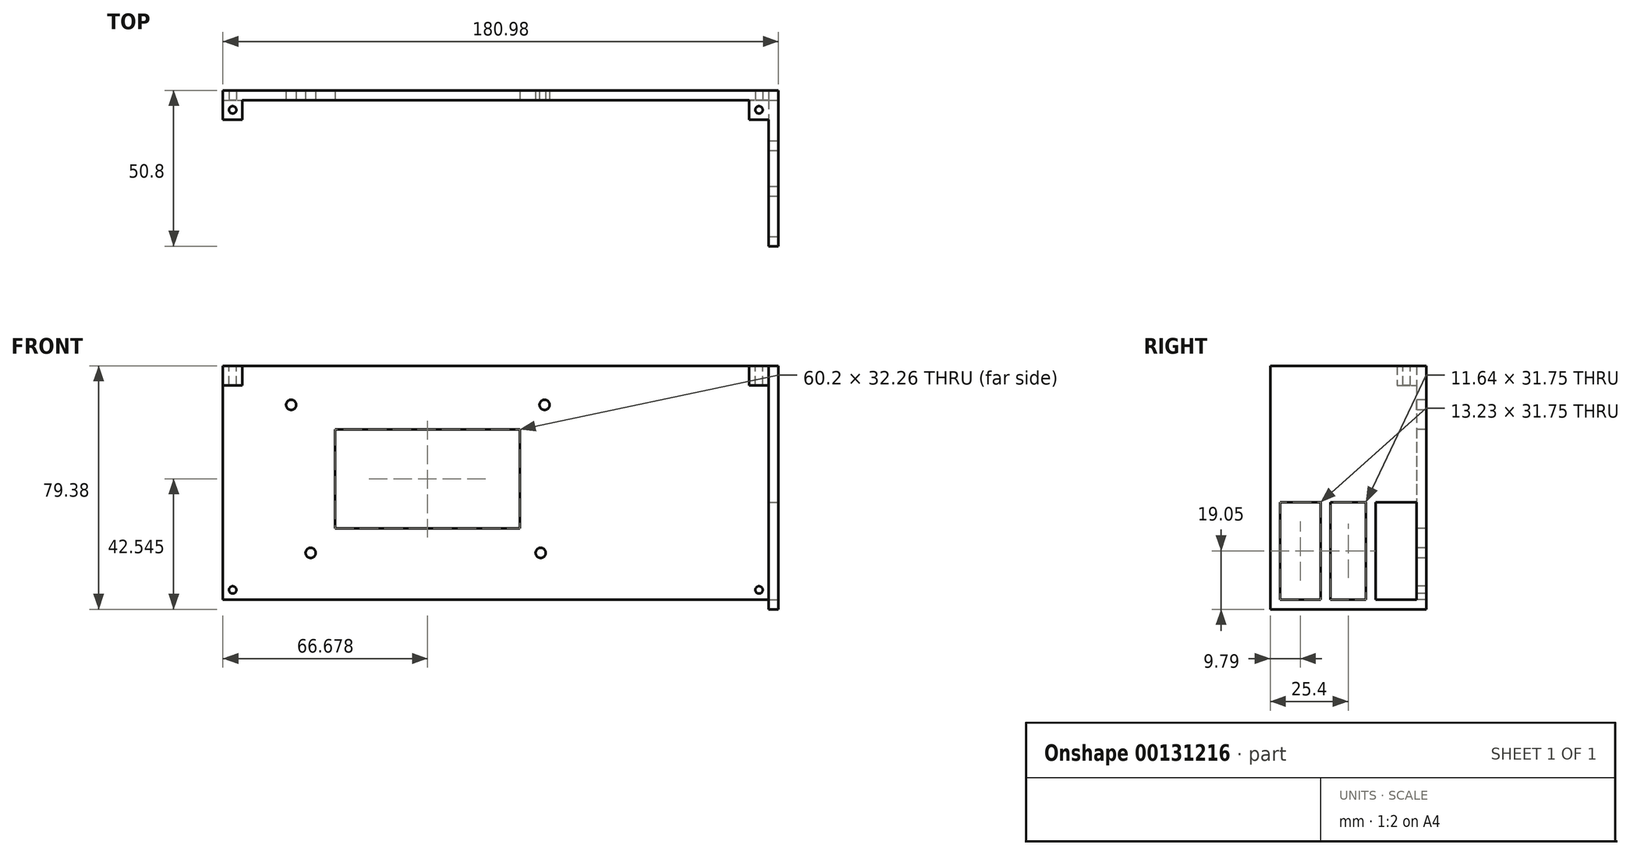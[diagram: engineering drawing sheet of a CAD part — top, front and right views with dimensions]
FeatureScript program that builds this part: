
annotation { "Feature Type Name" : "Feature", "Feature Type Description" : "" }
export const myFeature = defineFeature(function(context is Context, id is Id, definition is map)
    precondition{}
    {
        {
            var Q0;
            Q0=qCreatedBy(makeId("Top.planeOp"),FACE);
            var sketch = newSketch(context, id + "F0", { "sketchPlane" : qUnion([Q0])});
            skLineSegment(sketch, "E0.bottom", {"start": v(-95.97, 25.4) * mm, "end": v(88.18, 25.4) * mm});
            skLineSegment(sketch, "E0.top", {"start": v(-95.97, -25.4) * mm, "end": v(88.18, -25.4) * mm});
            skLineSegment(sketch, "E0.left", {"start": v(-95.97, 25.4) * mm, "end": v(-95.97, -25.4) * mm});
            skLineSegment(sketch, "E0.right", {"start": v(88.18, 25.4) * mm, "end": v(88.18, -25.4) * mm});
            skPoint(sketch, "E0.middle", {"position": v(-3.9, 0) * mm});
            skSolve(sketch);
        }
        {
            var Q0;
            Q0=makeQuery(id+"F0.imprint","IMPRINT",FACE,{"disambiguationData":[TD([[makeQuery(id+"F0.imprint","IMPRINT",EDGE,{"derivedFrom":sQuery(id+"F0.wireOp",EDGE,"E0.bottom")}),-1.0]])]});
            extrude(context, id + "F1", {"entities" : qUnion([Q0]), "depth" : 3.17 * mm});
        }
        {
            var Q0;
            Q0=makeQuery(id+"F1.opExtrude","CAP_FACE",FACE,{"disambiguationData":[OSD([sQuery(id+"F0.wireOp",EDGE,"E0.bottom"),sQuery(id+"F0.wireOp",EDGE,"E0.top"),sQuery(id+"F0.wireOp",EDGE,"E0.left"),sQuery(id+"F0.wireOp",EDGE,"E0.right")])],"isStart":false});
            var sketch = newSketch(context, id + "F2", { "sketchPlane" : qUnion([Q0])});
            skPoint(sketch, "E1", {"position": v(-78.9, 9.53) * mm});
            skPoint(sketch, "E2", {"position": v(71.1, 9.53) * mm});
            skPoint(sketch, "E3", {"position": v(71.1, -15.47) * mm});
            skPoint(sketch, "E4", {"position": v(-78.9, -15.47) * mm});
            skLineSegment(sketch, "E5", {"start": v(-78.9, 9.53) * mm, "end": v(-95.97, 9.53) * mm, "construction": true});
            skLineSegment(sketch, "E6", {"start": v(71.1, 9.53) * mm, "end": v(88.18, 9.53) * mm, "construction": true});
            skPoint(sketch, "E6.endSnap0", {"position": v(88.18, 0) * mm});
            skSolve(sketch);
        }
        {
            var Q0;
            Q0=sQuery(id+"F2.wireOp",VERTEX,"E1");
            var Q1;
            Q1=sQuery(id+"F2.wireOp",VERTEX,"E4");
            var Q2;
            Q2=sQuery(id+"F2.wireOp",VERTEX,"E3");
            var Q3;
            Q3=sQuery(id+"F2.wireOp",VERTEX,"E2");
            var Q4;
            Q4=makeQuery(id+"F1.opExtrude","SWEPT_BODY",BODY,{"disambiguationData":[OSD([sQuery(id+"F0.wireOp",EDGE,"E0.bottom"),sQuery(id+"F0.wireOp",EDGE,"E0.top"),sQuery(id+"F0.wireOp",EDGE,"E0.left"),sQuery(id+"F0.wireOp",EDGE,"E0.right")])]});
            hole(context, id + "F3", {"style" : HoleStyle.SIMPLE, "endStyle" : HoleEndStyle.THROUGH, "standardTappedOrClearance" : lookupTablePath({ "standard" : "ISO", "engagement" : "75%", "pitch" : "0.75 mm", "size" : "M4", "type" : "Tapped" }), "standardBlindInLast" : lookupTablePath({ "standard" : "ISO", "engagement" : "75%", "pitch" : "0.75 mm", "size" : "M4", "type" : "Tapped" }), "holeDiameter" : 3.2 * mm, "locations" : qUnion([Q0, Q1, Q2, Q3]), "scope" : qUnion([Q4]), "isTappedThrough" : true, "showTappedDepth" : true});
        }
        {
            var Q0;
            Q0=makeQuery(id+"F1.opExtrude","CAP_FACE",FACE,{"disambiguationData":[OSD([sQuery(id+"F0.wireOp",EDGE,"E0.bottom"),sQuery(id+"F0.wireOp",EDGE,"E0.top"),sQuery(id+"F0.wireOp",EDGE,"E0.left"),sQuery(id+"F0.wireOp",EDGE,"E0.right")])],"isStart":false});
            var sketch = newSketch(context, id + "F4", { "sketchPlane" : qUnion([Q0])});
            skLineSegment(sketch, "E7.bottom", {"start": v(-95.97, 25.4) * mm, "end": v(88.18, 25.4) * mm});
            skLineSegment(sketch, "E7.top", {"start": v(-95.97, 22.23) * mm, "end": v(88.18, 22.23) * mm});
            skLineSegment(sketch, "E7.left", {"start": v(-95.97, 25.4) * mm, "end": v(-95.97, 22.23) * mm});
            skLineSegment(sketch, "E7.right", {"start": v(88.18, 25.4) * mm, "end": v(88.18, 22.23) * mm});
            skSolve(sketch);
        }
        {
            var Q0;
            Q0=makeQuery(id+"F4.imprint","IMPRINT",FACE,{"disambiguationData":[TD([[makeQuery(id+"F4.imprint","IMPRINT",EDGE,{"derivedFrom":sQuery(id+"F4.wireOp",EDGE,"E7.bottom")}),-1.0]])]});
            extrude(context, id + "F5", {"entities" : qUnion([Q0]), "operationType" : NewBodyOperationType.ADD, "depth" : 76.2 * mm});
        }
        {
            var Q0;
            Q0=makeQuery(id+"F5.opExtrude","SWEPT_FACE",FACE,{"disambiguationData":[OSD([sQuery(id+"F4.wireOp",EDGE,"E7.top")])]});
            var sketch = newSketch(context, id + "F6", { "sketchPlane" : qUnion([Q0])});
            skPoint(sketch, "E8", {"position": v(-70.57, 66.67) * mm});
            skPoint(sketch, "E9", {"position": v(11.98, 66.67) * mm});
            skPoint(sketch, "E10", {"position": v(-64.22, 18.41) * mm});
            skPoint(sketch, "E11", {"position": v(10.7, 18.42) * mm});
            skSolve(sketch);
        }
        {
            var Q0;
            Q0=sQuery(id+"F6.wireOp",VERTEX,"E8");
            var Q1;
            Q1=sQuery(id+"F6.wireOp",VERTEX,"E9");
            var Q2;
            Q2=sQuery(id+"F6.wireOp",VERTEX,"E11");
            var Q3;
            Q3=sQuery(id+"F6.wireOp",VERTEX,"E10");
            var Q4;
            Q4=makeQuery(id+"F1.opExtrude","SWEPT_BODY",BODY,{"disambiguationData":[OSD([sQuery(id+"F0.wireOp",EDGE,"E0.bottom"),sQuery(id+"F0.wireOp",EDGE,"E0.top"),sQuery(id+"F0.wireOp",EDGE,"E0.left"),sQuery(id+"F0.wireOp",EDGE,"E0.right")])]});
            hole(context, id + "F7", {"style" : HoleStyle.SIMPLE, "endStyle" : HoleEndStyle.THROUGH, "standardTappedOrClearance" : lookupTablePath({ "standard" : "ISO", "fit" : "Normal", "size" : "M3", "type" : "Clearance" }), "standardBlindInLast" : lookupTablePath({ "fit" : "Standard", "standard" : "ISO", "size" : "M3", "type" : "Clearance" }), "holeDiameter" : 3.3 * mm, "locations" : qUnion([Q0, Q1, Q2, Q3]), "scope" : qUnion([Q4]), "isTappedThrough" : true});
        }
        {
            var Q0;
            Q0=makeQuery(id+"F1.opExtrude","CAP_FACE",FACE,{"disambiguationData":[OSD([sQuery(id+"F0.wireOp",EDGE,"E0.bottom"),sQuery(id+"F0.wireOp",EDGE,"E0.top"),sQuery(id+"F0.wireOp",EDGE,"E0.left"),sQuery(id+"F0.wireOp",EDGE,"E0.right")])],"isStart":false});
            var sketch = newSketch(context, id + "F8", { "sketchPlane" : qUnion([Q0])});
            skLineSegment(sketch, "E12.bottom", {"start": v(-95.97, 22.23) * mm, "end": v(-92.8, 22.23) * mm});
            skLineSegment(sketch, "E12.top", {"start": v(-95.97, -25.4) * mm, "end": v(-92.8, -25.4) * mm});
            skLineSegment(sketch, "E12.left", {"start": v(-95.97, 22.23) * mm, "end": v(-95.97, -25.4) * mm});
            skLineSegment(sketch, "E12.right", {"start": v(-92.8, 22.23) * mm, "end": v(-92.8, -25.4) * mm});
            skSolve(sketch);
        }
        {
            var Q0;
            Q0=makeQuery(id+"F8.imprint","IMPRINT",FACE,{"disambiguationData":[TD([[makeQuery(id+"F8.imprint","IMPRINT",EDGE,{"derivedFrom":sQuery(id+"F8.wireOp",EDGE,"E12.bottom")}),-1.0]])]});
            extrude(context, id + "F9", {"entities" : qUnion([Q0]), "operationType" : NewBodyOperationType.ADD, "depth" : 76.2 * mm});
        }
        {
            var Q0;
            Q0=makeQuery(id+"F9.boolean.opBoolean","MERGE",FACE,{"derivedFrom":[makeQuery(id+"F5.boolean.opBoolean","MERGE",FACE,{"derivedFrom":[makeQuery(id+"F1.opExtrude","SWEPT_FACE",FACE,{"disambiguationData":[OSD([sQuery(id+"F0.wireOp",EDGE,"E0.left")])]}),makeQuery(id+"F5.opExtrude","SWEPT_FACE",FACE,{"disambiguationData":[OSD([sQuery(id+"F4.wireOp",EDGE,"E7.left")])]})]}),makeQuery(id+"F9.opExtrude","SWEPT_FACE",FACE,{"disambiguationData":[OSD([sQuery(id+"F8.wireOp",EDGE,"E12.left")])]})]});
            var sketch = newSketch(context, id + "F10", { "sketchPlane" : qUnion([Q0])});
            skLineSegment(sketch, "E13.bottom", {"start": v(3.18, 76.2) * mm, "end": v(22.23, 76.2) * mm});
            skLineSegment(sketch, "E13.top", {"start": v(3.18, 3.18) * mm, "end": v(22.23, 3.18) * mm});
            skLineSegment(sketch, "E13.left", {"start": v(3.18, 76.2) * mm, "end": v(3.18, 3.17) * mm});
            skLineSegment(sketch, "E13.right", {"start": v(22.23, 76.2) * mm, "end": v(22.23, 3.17) * mm});
            skLineSegment(sketch, "E14", {"start": v(3.18, 39.69) * mm, "end": v(22.23, 39.69) * mm});
            skLineSegment(sketch, "E15", {"start": v(3.18, 41.27) * mm, "end": v(22.23, 41.27) * mm});
            skLineSegment(sketch, "E16", {"start": v(3.18, 38.1) * mm, "end": v(22.23, 38.1) * mm});
            skSolve(sketch);
        }
        {
            var Q0;
            {var subQ0=sQuery(id+"F10.wireOp",EDGE,"E13.bottom");Q0=makeQuery(id+"F10.imprint","IMPRINT",FACE,{"disambiguationData":[TD([[makeQuery(id+"F10.imprint","IMPRINT",EDGE,{"derivedFrom":subQ0}),-1.0]])]});}
            var Q1;
            {var subQ0=sQuery(id+"F10.wireOp",EDGE,"E13.top");Q1=makeQuery(id+"F10.imprint","IMPRINT",FACE,{"disambiguationData":[TD([[makeQuery(id+"F10.imprint","IMPRINT",EDGE,{"derivedFrom":subQ0}),1.0]])]});}
            extrude(context, id + "F11", {"entities" : qUnion([Q0, Q1]), "operationType" : NewBodyOperationType.REMOVE, "endBound" : BoundingType.UP_TO_NEXT, "oppositeDirection" : true, "depth" : 25.4 * mm});
        }
        {
            var Q0;
            Q0=makeQuery(id+"F11.boolean.opBoolean","MERGE",FACE,{"derivedFrom":[makeQuery(id+"F1.opExtrude","CAP_FACE",FACE,{"disambiguationData":[OSD([sQuery(id+"F0.wireOp",EDGE,"E0.bottom"),sQuery(id+"F0.wireOp",EDGE,"E0.top"),sQuery(id+"F0.wireOp",EDGE,"E0.left"),sQuery(id+"F0.wireOp",EDGE,"E0.right")])],"isStart":false}),makeQuery(id+"F11.opExtrude","SWEPT_FACE",FACE,{"disambiguationData":[OSD([sQuery(id+"F10.wireOp",EDGE,"E13.top")])]})]});
            var sketch = newSketch(context, id + "F12", { "sketchPlane" : qUnion([Q0])});
            skLineSegment(sketch, "E17.bottom", {"start": v(88.18, 22.23) * mm, "end": v(85, 22.23) * mm});
            skLineSegment(sketch, "E17.top", {"start": v(88.18, -25.4) * mm, "end": v(85, -25.4) * mm});
            skLineSegment(sketch, "E17.left", {"start": v(88.18, 22.23) * mm, "end": v(88.18, -25.4) * mm});
            skLineSegment(sketch, "E17.right", {"start": v(85, 22.23) * mm, "end": v(85, -25.4) * mm});
            skSolve(sketch);
        }
        {
            var Q0;
            Q0=makeQuery(id+"F12.imprint","IMPRINT",FACE,{"disambiguationData":[TD([[makeQuery(id+"F12.imprint","IMPRINT",EDGE,{"derivedFrom":sQuery(id+"F12.wireOp",EDGE,"E17.bottom")}),-1.0]])]});
            extrude(context, id + "F13", {"entities" : qUnion([Q0]), "operationType" : NewBodyOperationType.ADD, "depth" : 76.2 * mm});
        }
        {
            var Q0;
            Q0=makeQuery(id+"F13.boolean.opBoolean","MERGE",FACE,{"derivedFrom":[makeQuery(id+"F5.boolean.opBoolean","MERGE",FACE,{"derivedFrom":[makeQuery(id+"F1.opExtrude","SWEPT_FACE",FACE,{"disambiguationData":[OSD([sQuery(id+"F0.wireOp",EDGE,"E0.right")])]}),makeQuery(id+"F5.opExtrude","SWEPT_FACE",FACE,{"disambiguationData":[OSD([sQuery(id+"F4.wireOp",EDGE,"E7.right")])]})]}),makeQuery(id+"F13.opExtrude","SWEPT_FACE",FACE,{"disambiguationData":[OSD([sQuery(id+"F12.wireOp",EDGE,"E17.left")])]})]});
            var sketch = newSketch(context, id + "F14", { "sketchPlane" : qUnion([Q0])});
            skLineSegment(sketch, "E18.bottom", {"start": v(-22.22, 3.17) * mm, "end": v(22.23, 3.18) * mm});
            skLineSegment(sketch, "E18.top", {"start": v(-22.22, 34.92) * mm, "end": v(22.23, 34.93) * mm});
            skLineSegment(sketch, "E18.left", {"start": v(-22.22, 3.17) * mm, "end": v(-22.22, 34.92) * mm});
            skLineSegment(sketch, "E18.right", {"start": v(22.23, 3.17) * mm, "end": v(22.23, 34.92) * mm});
            skLineSegment(sketch, "E19", {"start": v(-7.4, 34.92) * mm, "end": v(-7.4, 3.18) * mm, "construction": true});
            skLineSegment(sketch, "E20", {"start": v(7.4, 34.92) * mm, "end": v(7.4, 3.18) * mm, "construction": true});
            skLineSegment(sketch, "E21", {"start": v(-22.22, 19.05) * mm, "end": v(-7.4, 19.05) * mm, "construction": true});
            skLineSegment(sketch, "E22", {"start": v(-7.4, 19.05) * mm, "end": v(7.4, 19.05) * mm, "construction": true});
            skLineSegment(sketch, "E23", {"start": v(7.4, 19.05) * mm, "end": v(22.23, 19.05) * mm, "construction": true});
            skLineSegment(sketch, "E24.bottom", {"start": v(-9, 34.92) * mm, "end": v(-5.82, 34.92) * mm});
            skLineSegment(sketch, "E24.top", {"start": v(-9, 3.17) * mm, "end": v(-5.82, 3.17) * mm});
            skLineSegment(sketch, "E24.left", {"start": v(-9, 34.92) * mm, "end": v(-9, 3.17) * mm});
            skLineSegment(sketch, "E24.right", {"start": v(-5.82, 34.92) * mm, "end": v(-5.82, 3.17) * mm});
            skPoint(sketch, "E24.middle", {"position": v(-7.4, 19.05) * mm});
            skLineSegment(sketch, "E25.bottom", {"start": v(5.82, 34.92) * mm, "end": v(9, 34.92) * mm});
            skLineSegment(sketch, "E25.top", {"start": v(5.82, 3.17) * mm, "end": v(9, 3.17) * mm});
            skLineSegment(sketch, "E25.left", {"start": v(5.82, 34.92) * mm, "end": v(5.82, 3.17) * mm});
            skLineSegment(sketch, "E25.right", {"start": v(9, 34.92) * mm, "end": v(9, 3.17) * mm});
            skPoint(sketch, "E25.middle", {"position": v(7.4, 19.05) * mm});
            skSolve(sketch);
        }
        {
            var Q0;
            {var subQ0=sQuery(id+"F14.wireOp",EDGE,"E18.left");Q0=makeQuery(id+"F14.imprint","IMPRINT",FACE,{"disambiguationData":[TD([[makeQuery(id+"F14.imprint","IMPRINT",EDGE,{"derivedFrom":subQ0}),-1.0]])]});}
            var Q1;
            {var subQ0=sQuery(id+"F14.wireOp",EDGE,"E24.right");Q1=makeQuery(id+"F14.imprint","IMPRINT",FACE,{"disambiguationData":[TD([[makeQuery(id+"F14.imprint","IMPRINT",EDGE,{"derivedFrom":subQ0}),1.0]])]});}
            var Q2;
            {var subQ0=sQuery(id+"F14.wireOp",EDGE,"E18.right");Q2=makeQuery(id+"F14.imprint","IMPRINT",FACE,{"disambiguationData":[TD([[makeQuery(id+"F14.imprint","IMPRINT",EDGE,{"derivedFrom":subQ0}),1.0]])]});}
            extrude(context, id + "F15", {"entities" : qUnion([Q0, Q1, Q2]), "operationType" : NewBodyOperationType.REMOVE, "endBound" : BoundingType.UP_TO_NEXT, "oppositeDirection" : true, "depth" : 25.4 * mm});
        }
        {
            var Q0;
            Q0=makeQuery(id+"F15.boolean.opBoolean","MERGE",FACE,{"derivedFrom":[makeQuery(id+"F5.opExtrude","SWEPT_FACE",FACE,{"disambiguationData":[OSD([sQuery(id+"F4.wireOp",EDGE,"E7.top")])]}),makeQuery(id+"F15.opExtrude","SWEPT_FACE",FACE,{"disambiguationData":[OSD([sQuery(id+"F14.wireOp",EDGE,"E18.right")])]})]});
            var sketch = newSketch(context, id + "F16", { "sketchPlane" : qUnion([Q0])});
            skLineSegment(sketch, "E26.bottom", {"start": v(-92.8, 79.38) * mm, "end": v(-86.45, 79.38) * mm});
            skLineSegment(sketch, "E26.top", {"start": v(-92.8, 73.03) * mm, "end": v(-86.45, 73.03) * mm});
            skLineSegment(sketch, "E26.left", {"start": v(-92.8, 79.38) * mm, "end": v(-92.8, 73.03) * mm});
            skLineSegment(sketch, "E26.right", {"start": v(-86.45, 79.38) * mm, "end": v(-86.45, 73.03) * mm});
            skLineSegment(sketch, "E27.bottom", {"start": v(85, 79.38) * mm, "end": v(78.65, 79.38) * mm});
            skLineSegment(sketch, "E27.top", {"start": v(85, 73.03) * mm, "end": v(78.65, 73.03) * mm});
            skLineSegment(sketch, "E27.left", {"start": v(85, 79.38) * mm, "end": v(85, 73.03) * mm});
            skLineSegment(sketch, "E27.right", {"start": v(78.65, 79.38) * mm, "end": v(78.65, 73.03) * mm});
            skSolve(sketch);
        }
        {
            var Q0;
            Q0=makeQuery(id+"F16.imprint","IMPRINT",FACE,{"disambiguationData":[TD([[makeQuery(id+"F16.imprint","IMPRINT",EDGE,{"derivedFrom":sQuery(id+"F16.wireOp",EDGE,"E26.bottom")}),-1.0]])]});
            var Q1;
            Q1=makeQuery(id+"F16.imprint","IMPRINT",FACE,{"disambiguationData":[TD([[makeQuery(id+"F16.imprint","IMPRINT",EDGE,{"derivedFrom":sQuery(id+"F16.wireOp",EDGE,"E26.bottom")}),-1.0]])]});
            var Q2;
            Q2=makeQuery(id+"F16.imprint","IMPRINT",FACE,{"disambiguationData":[TD([[makeQuery(id+"F16.imprint","IMPRINT",EDGE,{"derivedFrom":sQuery(id+"F16.wireOp",EDGE,"E27.bottom")}),-1.0]])]});
            extrude(context, id + "F17", {"entities" : qUnion([Q0, Q1, Q2]), "operationType" : NewBodyOperationType.ADD, "depth" : 6.35 * mm});
        }
        {
            var Q0;
            Q0=makeQuery(id+"F17.boolean.opBoolean","MERGE",FACE,{"derivedFrom":[makeQuery(id+"F13.boolean.opBoolean","MERGE",FACE,{"derivedFrom":[makeQuery(id+"F9.boolean.opBoolean","MERGE",FACE,{"derivedFrom":[makeQuery(id+"F5.opExtrude","CAP_FACE",FACE,{"disambiguationData":[OSD([sQuery(id+"F4.wireOp",EDGE,"E7.bottom"),sQuery(id+"F4.wireOp",EDGE,"E7.top"),sQuery(id+"F4.wireOp",EDGE,"E7.left"),sQuery(id+"F4.wireOp",EDGE,"E7.right")])],"isStart":false}),makeQuery(id+"F9.opExtrude","CAP_FACE",FACE,{"disambiguationData":[OSD([sQuery(id+"F8.wireOp",EDGE,"E12.bottom"),sQuery(id+"F8.wireOp",EDGE,"E12.top"),sQuery(id+"F8.wireOp",EDGE,"E12.left"),sQuery(id+"F8.wireOp",EDGE,"E12.right")])],"isStart":false})]}),makeQuery(id+"F13.opExtrude","CAP_FACE",FACE,{"disambiguationData":[OSD([sQuery(id+"F12.wireOp",EDGE,"E17.bottom"),sQuery(id+"F12.wireOp",EDGE,"E17.top"),sQuery(id+"F12.wireOp",EDGE,"E17.left"),sQuery(id+"F12.wireOp",EDGE,"E17.right")])],"isStart":false})]}),makeQuery(id+"F17.opExtrude","SWEPT_FACE",FACE,{"disambiguationData":[OSD([sQuery(id+"F16.wireOp",EDGE,"E26.bottom")])]}),makeQuery(id+"F17.opExtrude","SWEPT_FACE",FACE,{"disambiguationData":[OSD([sQuery(id+"F16.wireOp",EDGE,"E27.bottom")])]})]});
            var sketch = newSketch(context, id + "F18", { "sketchPlane" : qUnion([Q0])});
            skPoint(sketch, "E28", {"position": v(-89.62, 19.05) * mm});
            skPoint(sketch, "E29", {"position": v(81.83, 19.05) * mm});
            skSolve(sketch);
        }
        {
            var Q0;
            Q0=sQuery(id+"F18.wireOp",VERTEX,"E28");
            var Q1;
            Q1=sQuery(id+"F18.wireOp",VERTEX,"E29");
            var Q2;
            Q2=makeQuery(id+"F1.opExtrude","SWEPT_BODY",BODY,{"disambiguationData":[OSD([sQuery(id+"F0.wireOp",EDGE,"E0.bottom"),sQuery(id+"F0.wireOp",EDGE,"E0.top"),sQuery(id+"F0.wireOp",EDGE,"E0.left"),sQuery(id+"F0.wireOp",EDGE,"E0.right")])]});
            hole(context, id + "F19", {"style" : HoleStyle.SIMPLE, "endStyle" : HoleEndStyle.BLIND, "standardTappedOrClearance" : lookupTablePath({ "standard" : "ISO", "engagement" : "75%", "pitch" : "0.6 mm", "size" : "M3", "type" : "Tapped" }), "standardBlindInLast" : lookupTablePath({ "standard" : "ISO", "engagement" : "75%", "pitch" : "0.6 mm", "size" : "M3", "type" : "Tapped" }), "holeDiameter" : 2.4 * mm, "holeDepth" : 12.7 * mm, "locations" : qUnion([Q0, Q1]), "scope" : qUnion([Q2])});
        }
        {
            var Q0;
            {var subQ0=sQuery(id+"F14.wireOp",EDGE,"E18.bottom");var subQ2=sQuery(id+"F14.wireOp",EDGE,"E24.top");Q0=makeQuery(id+"F15.boolean.opBoolean","MERGE",FACE,{"derivedFrom":[makeQuery(id+"F11.boolean.opBoolean","MERGE",FACE,{"derivedFrom":[makeQuery(id+"F1.opExtrude","CAP_FACE",FACE,{"disambiguationData":[OSD([sQuery(id+"F0.wireOp",EDGE,"E0.bottom"),sQuery(id+"F0.wireOp",EDGE,"E0.top"),sQuery(id+"F0.wireOp",EDGE,"E0.left"),sQuery(id+"F0.wireOp",EDGE,"E0.right")])],"isStart":false}),makeQuery(id+"F11.opExtrude","SWEPT_FACE",FACE,{"disambiguationData":[OSD([sQuery(id+"F10.wireOp",EDGE,"E13.top")])]})]}),makeQuery(id+"F15.opExtrude","SWEPT_FACE",FACE,{"disambiguationData":[OSD([subQ0]),TDD([makeQuery(id+"F14.imprint","IMPRINT",EDGE,{"disambiguationData":[TD([[makeQuery(id+"F14.imprint","INTERSECT",VERTEX,{"derivedFrom":[subQ0,sQuery(id+"F14.wireOp",EDGE,"E18.left")]}),-1.0]])],"derivedFrom":subQ0})])]}),makeQuery(id+"F15.opExtrude","SWEPT_FACE",FACE,{"disambiguationData":[OSD([subQ0]),TDD([makeQuery(id+"F14.imprint","IMPRINT",EDGE,{"disambiguationData":[TD([[makeQuery(id+"F14.imprint","INTERSECT",VERTEX,{"derivedFrom":[subQ0,subQ2,sQuery(id+"F14.wireOp",EDGE,"E24.right")]}),-1.0]])],"derivedFrom":subQ0})])]}),makeQuery(id+"F15.opExtrude","SWEPT_FACE",FACE,{"disambiguationData":[OSD([subQ0]),TDD([makeQuery(id+"F14.imprint","IMPRINT",EDGE,{"disambiguationData":[TD([[makeQuery(id+"F14.imprint","INTERSECT",VERTEX,{"derivedFrom":[subQ0,sQuery(id+"F14.wireOp",EDGE,"E18.right")]}),1.0]])],"derivedFrom":subQ0})])]})]});}
            var sketch = newSketch(context, id + "F20", { "sketchPlane" : qUnion([Q0])});
            skLineSegment(sketch, "E30.bottom", {"start": v(-64.6, -19.05) * mm, "end": v(56.8, -19.05) * mm});
            skLineSegment(sketch, "E30.top", {"start": v(-64.6, 15.88) * mm, "end": v(56.8, 15.88) * mm});
            skLineSegment(sketch, "E30.left", {"start": v(-64.6, -19.05) * mm, "end": v(-64.6, 15.88) * mm});
            skLineSegment(sketch, "E30.right", {"start": v(56.8, -19.05) * mm, "end": v(56.8, 15.88) * mm});
            skSolve(sketch);
        }
        {
            var Q0;
            Q0=makeQuery(id+"F20.imprint","IMPRINT",FACE,{"disambiguationData":[TD([[makeQuery(id+"F20.imprint","IMPRINT",EDGE,{"derivedFrom":sQuery(id+"F20.wireOp",EDGE,"E30.bottom")}),1.0]])]});
            extrude(context, id + "F21", {"entities" : qUnion([Q0]), "operationType" : NewBodyOperationType.REMOVE, "oppositeDirection" : true, "depth" : 25.4 * mm});
        }
        {
            var Q0;
            Q0=makeQuery(id+"F15.boolean.opBoolean","MERGE",FACE,{"derivedFrom":[makeQuery(id+"F5.opExtrude","SWEPT_FACE",FACE,{"disambiguationData":[OSD([sQuery(id+"F4.wireOp",EDGE,"E7.top")])]}),makeQuery(id+"F15.opExtrude","SWEPT_FACE",FACE,{"disambiguationData":[OSD([sQuery(id+"F14.wireOp",EDGE,"E18.right")])]})]});
            var sketch = newSketch(context, id + "F22", { "sketchPlane" : qUnion([Q0])});
            skLineSegment(sketch, "E31.bottom", {"start": v(-56.22, 58.67) * mm, "end": v(3.98, 58.67) * mm});
            skLineSegment(sketch, "E31.top", {"start": v(-56.22, 26.42) * mm, "end": v(3.98, 26.42) * mm});
            skLineSegment(sketch, "E31.left", {"start": v(-56.22, 58.67) * mm, "end": v(-56.22, 26.42) * mm});
            skLineSegment(sketch, "E31.right", {"start": v(3.98, 58.67) * mm, "end": v(3.98, 26.42) * mm});
            skSolve(sketch);
        }
        {
            var Q0;
            Q0=makeQuery(id+"F22.imprint","IMPRINT",FACE,{"disambiguationData":[TD([[makeQuery(id+"F22.imprint","IMPRINT",EDGE,{"derivedFrom":sQuery(id+"F22.wireOp",EDGE,"E31.bottom")}),-1.0]])]});
            extrude(context, id + "F23", {"entities" : qUnion([Q0]), "operationType" : NewBodyOperationType.REMOVE, "oppositeDirection" : true, "depth" : 25.4 * mm});
        }
        {
            var Q0;
            Q0=makeQuery(id+"F13.boolean.opBoolean","MERGE",FACE,{"derivedFrom":[makeQuery(id+"F9.boolean.opBoolean","MERGE",FACE,{"derivedFrom":[makeQuery(id+"F1.opExtrude","SWEPT_FACE",FACE,{"disambiguationData":[OSD([sQuery(id+"F0.wireOp",EDGE,"E0.top")])]}),makeQuery(id+"F9.opExtrude","SWEPT_FACE",FACE,{"disambiguationData":[OSD([sQuery(id+"F8.wireOp",EDGE,"E12.top")])]})]}),makeQuery(id+"F13.opExtrude","SWEPT_FACE",FACE,{"disambiguationData":[OSD([sQuery(id+"F12.wireOp",EDGE,"E17.top")])]})]});
            var sketch = newSketch(context, id + "F24", { "sketchPlane" : qUnion([Q0])});
            skLineSegment(sketch, "E32", {"start": v(-95.97, 79.38) * mm, "end": v(-92.8, 79.38) * mm});
            skLineSegment(sketch, "E33", {"start": v(-92.8, 79.38) * mm, "end": v(-92.8, 3.17) * mm});
            skLineSegment(sketch, "E34", {"start": v(-92.8, 3.17) * mm, "end": v(85, 3.18) * mm});
            skLineSegment(sketch, "E35", {"start": v(85, 3.18) * mm, "end": v(85, 0) * mm});
            skLineSegment(sketch, "E36", {"start": v(85, 0) * mm, "end": v(-95.97, 0) * mm});
            skLineSegment(sketch, "E37", {"start": v(-95.97, 0) * mm, "end": v(-95.97, 79.38) * mm});
            skSolve(sketch);
        }
        {
            var Q0;
            Q0=makeQuery(id+"F24.imprint","IMPRINT",FACE,{"disambiguationData":[TD([[makeQuery(id+"F24.imprint","IMPRINT",EDGE,{"derivedFrom":sQuery(id+"F24.wireOp",EDGE,"E32")}),-1.0]])]});
            extrude(context, id + "F25", {"entities" : qUnion([Q0]), "operationType" : NewBodyOperationType.REMOVE, "endBound" : BoundingType.THROUGH_ALL, "oppositeDirection" : true, "depth" : 25.4 * mm});
        }
        {
            var Q0;
            Q0=makeQuery(id+"F15.boolean.opBoolean","MERGE",FACE,{"derivedFrom":[makeQuery(id+"F5.opExtrude","SWEPT_FACE",FACE,{"disambiguationData":[OSD([sQuery(id+"F4.wireOp",EDGE,"E7.top")])]}),makeQuery(id+"F15.opExtrude","SWEPT_FACE",FACE,{"disambiguationData":[OSD([sQuery(id+"F14.wireOp",EDGE,"E18.right")])]})]});
            var sketch = newSketch(context, id + "F26", { "sketchPlane" : qUnion([Q0])});
            skPoint(sketch, "E38", {"position": v(-89.62, 6.35) * mm});
            skPoint(sketch, "E39", {"position": v(81.83, 6.35) * mm});
            skSolve(sketch);
        }
        {
            var Q0;
            Q0=sQuery(id+"F26.wireOp",VERTEX,"E38");
            var Q1;
            Q1=sQuery(id+"F26.wireOp",VERTEX,"E39");
            var Q2;
            Q2=makeQuery(id+"F1.opExtrude","SWEPT_BODY",BODY,{"disambiguationData":[OSD([sQuery(id+"F0.wireOp",EDGE,"E0.bottom"),sQuery(id+"F0.wireOp",EDGE,"E0.top"),sQuery(id+"F0.wireOp",EDGE,"E0.left"),sQuery(id+"F0.wireOp",EDGE,"E0.right")])]});
            hole(context, id + "F27", {"style" : HoleStyle.SIMPLE, "endStyle" : HoleEndStyle.BLIND, "standardTappedOrClearance" : lookupTablePath({ "standard" : "ISO", "engagement" : "75%", "pitch" : "0.6 mm", "size" : "M3", "type" : "Tapped" }), "standardBlindInLast" : lookupTablePath({ "standard" : "ISO", "engagement" : "75%", "pitch" : "0.6 mm", "size" : "M3", "type" : "Tapped" }), "holeDiameter" : 2.4 * mm, "holeDepth" : 12.7 * mm, "locations" : qUnion([Q0, Q1]), "scope" : qUnion([Q2])});
        }
    });
